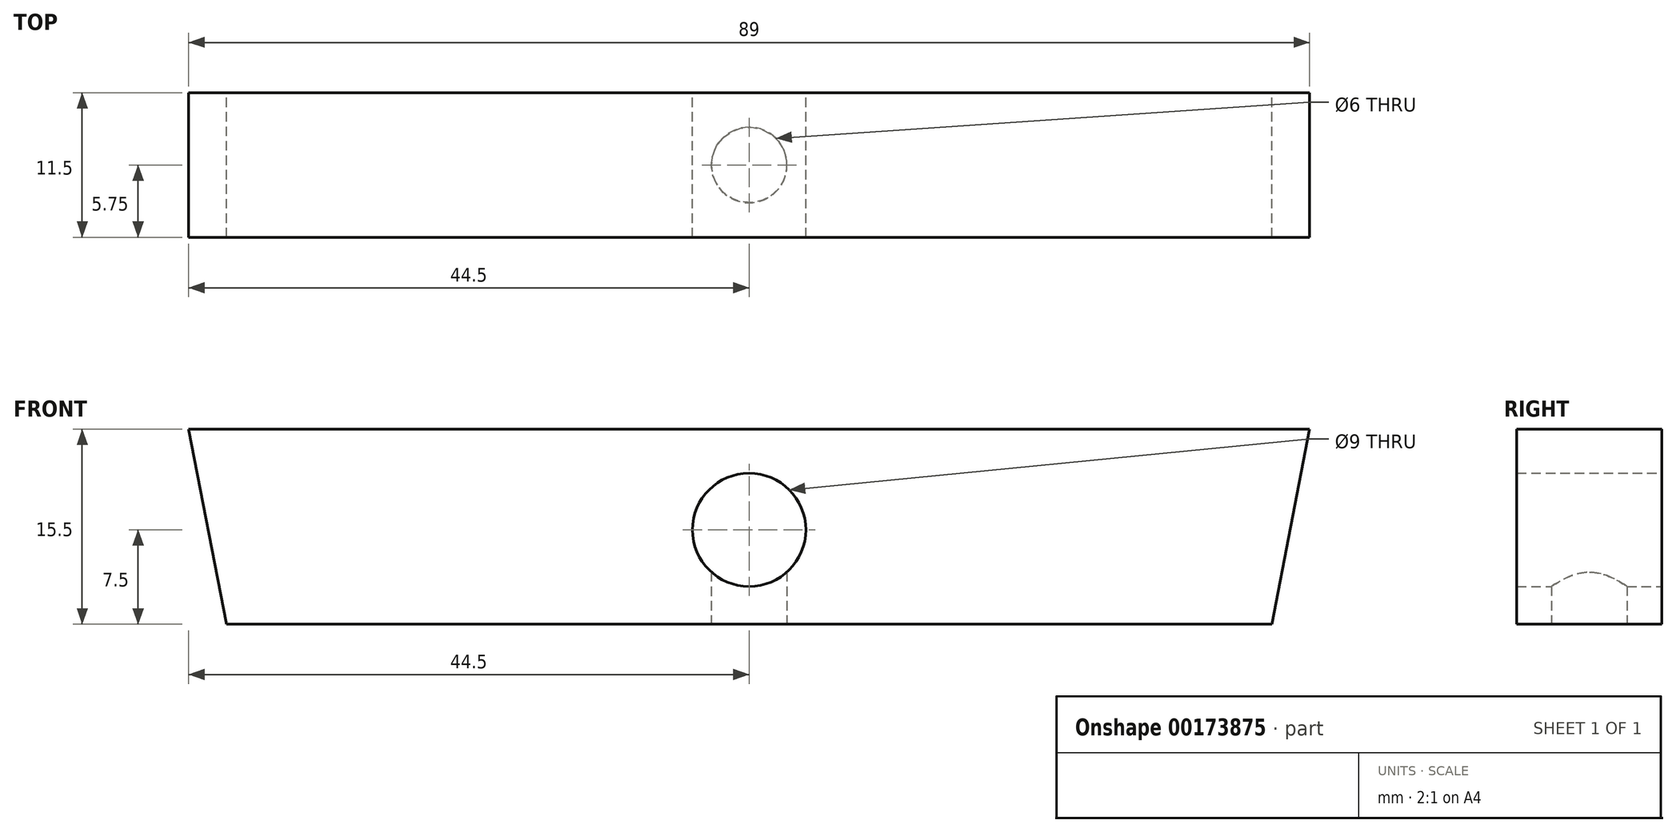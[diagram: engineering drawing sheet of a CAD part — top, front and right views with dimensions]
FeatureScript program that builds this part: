
annotation { "Feature Type Name" : "Feature", "Feature Type Description" : "" }
export const myFeature = defineFeature(function(context is Context, id is Id, definition is map)
    precondition{}
    {
        {
            var Q0;
            Q0=qCreatedBy(makeId("Front.planeOp"),FACE);
            var sketch = newSketch(context, id + "F0", { "sketchPlane" : qUnion([Q0])});
            skLineSegment(sketch, "E0", {"start": v(-41.5, 0) * mm, "end": v(41.5, 0) * mm});
            skLineSegment(sketch, "E1", {"start": v(41.5, 0) * mm, "end": v(44.5, 15.5) * mm});
            skLineSegment(sketch, "E2", {"start": v(44.5, 15.5) * mm, "end": v(-44.5, 15.5) * mm});
            skLineSegment(sketch, "E3", {"start": v(-44.5, 15.5) * mm, "end": v(-41.5, 0) * mm});
            skSolve(sketch);
        }
        {
            var Q0;
            Q0=qSketchRegion(id+"F0",true);
            extrude(context, id + "F1", {"entities" : qUnion([Q0]), "depth" : 11.5 * mm});
        }
        {
            var Q0;
            Q0=makeQuery(id+"F1.opExtrude","CAP_FACE",FACE,{"disambiguationData":[OSD([sQuery(id+"F0.wireOp",EDGE,"E0"),sQuery(id+"F0.wireOp",EDGE,"E1"),sQuery(id+"F0.wireOp",EDGE,"E2"),sQuery(id+"F0.wireOp",EDGE,"E3")])],"isStart":true});
            var sketch = newSketch(context, id + "F2", { "sketchPlane" : qUnion([Q0])});
            skCircle(sketch, "E4", {"center": v(0, 7.5) * mm, "radius": 4.5 * mm});
            skSolve(sketch);
        }
        {
            var Q0;
            Q0=qSketchRegion(id+"F2",true);
            extrude(context, id + "F3", {"entities" : qUnion([Q0]), "operationType" : NewBodyOperationType.REMOVE, "endBound" : BoundingType.THROUGH_ALL, "oppositeDirection" : true, "depth" : 25 * mm});
        }
        {
            var Q0;
            Q0=makeQuery(id+"F1.opExtrude","SWEPT_FACE",FACE,{"disambiguationData":[OSD([sQuery(id+"F0.wireOp",EDGE,"E0")])]});
            var sketch = newSketch(context, id + "F4", { "sketchPlane" : qUnion([Q0])});
            skLineSegment(sketch, "E5", {"start": v(0, 0) * mm, "end": v(0, 11.5) * mm, "construction": true});
            skCircle(sketch, "E6", {"center": v(0, 5.75) * mm, "radius": 3 * mm});
            skSolve(sketch);
        }
        {
            var Q0;
            Q0=qSketchRegion(id+"F4",true);
            extrude(context, id + "F5", {"entities" : qUnion([Q0]), "operationType" : NewBodyOperationType.REMOVE, "oppositeDirection" : true, "depth" : 10 * mm});
        }
    });
